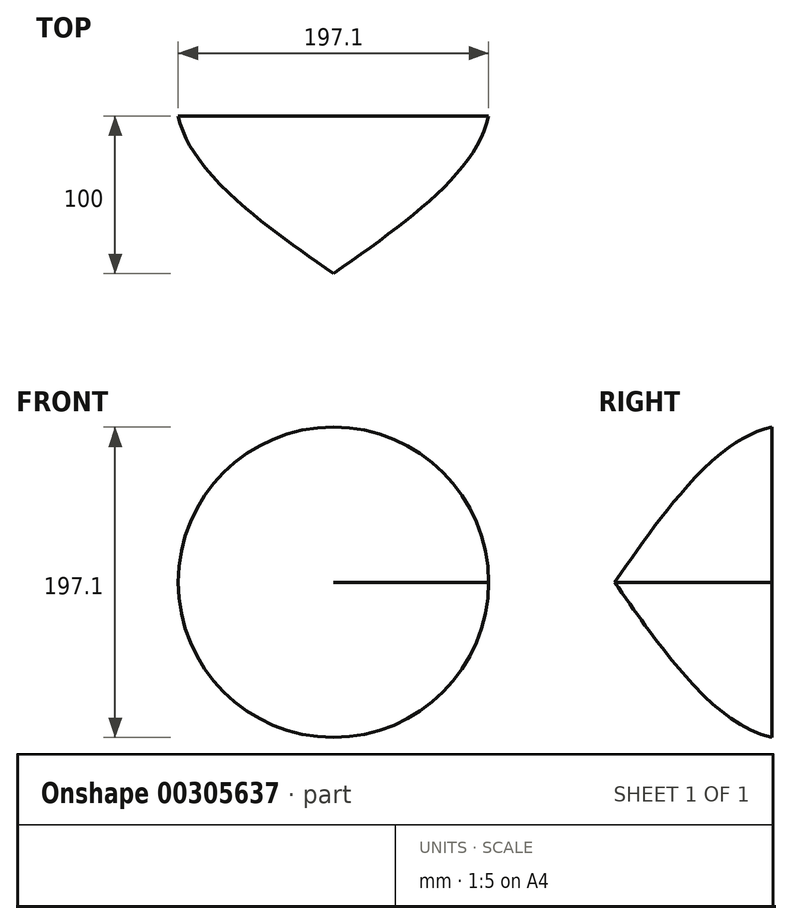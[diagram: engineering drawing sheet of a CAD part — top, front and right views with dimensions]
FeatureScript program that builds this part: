
annotation { "Feature Type Name" : "Feature", "Feature Type Description" : "" }
export const myFeature = defineFeature(function(context is Context, id is Id, definition is map)
    precondition{}
    {
        {
            var Q0;
            Q0=qCreatedBy(makeId("Top.planeOp"),FACE);
            var sketch = newSketch(context, id + "F0", { "sketchPlane" : qUnion([Q0])});
            skLineSegment(sketch, "E0", {"start": v(0, 0) * mm, "end": v(0, 100) * mm});
            skLineSegment(sketch, "E1", {"start": v(0, 0) * mm, "end": v(0, -100) * mm});
            skLineSegment(sketch, "E2", {"start": v(0, 0) * mm, "end": v(100, 0) * mm});
            skFitSpline(sketch, "E3", {"points": [v(0, 100) * mm, v(48.8, 90.61) * mm, v(99.65, 7.77) * mm, v(0, -100) * mm], "startDerivative": vector(192.91, 6.42) * mm, "endDerivative": vector(-348.87, -244.75) * mm});
            skSolve(sketch);
        }
        {
            var Q0;
            {var subQ0=sQuery(id+"F0.wireOp",EDGE,"E1");Q0=makeQuery(id+"F0.imprint","IMPRINT",FACE,{"disambiguationData":[TD([[makeQuery(id+"F0.imprint","IMPRINT",EDGE,{"derivedFrom":subQ0}),1.0]])]});}
            var Q1;
            Q1=sQuery(id+"F0.wireOp",EDGE,"E1");
            revolve(context, id + "F1", {"entities" : qUnion([Q0]), "axis" : qUnion([Q1]), "revolveType" : RevolveType.FULL});
        }
    });
